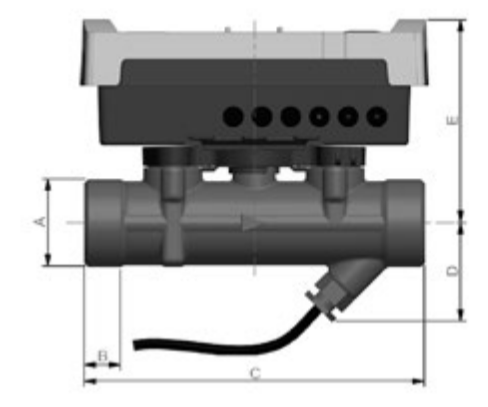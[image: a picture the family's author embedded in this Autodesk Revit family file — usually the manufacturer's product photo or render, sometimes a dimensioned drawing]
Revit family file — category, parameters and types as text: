
# Revit family: Узел квартирный для ГВС и ХВС_Danfoss_ШКСВ
name_source: partatom
category: Арматура трубопроводов
revit_build: Autodesk Revit 2018 (Build: 20170223_1515(x64)
units: mm (PartAtom-declared; Revit-internal decimal feet)

## family parameters
Всегда вертикально = Да
На основе рабочей плоскости = Нет
Общий = Нет
При загрузке вырезать с полостями = Нет
Размер круглого соединителя = Использовать диаметр
Тип детали = Нормальный

## types (2) — shared parameters
ADSK_Единица измерения = шт.
ADSK_Завод-изготовитель = Danfoss
ADSK_Количество = 1
ADSK_Материал = Danfoss__Сталь
URL = https://www.danfoss.com
Изготовитель = Danfoss
Изготовитель (телефон) = +7(495)792-57-57
Разработчик = ООО ПРОРУБИМ
Разработчик (URL) = http://prorubim.com
Разработчик (телефон) = +7(495)649-85-43
Таблица1 = ШКСВ_Обозначение
Таблица2 = ШКСВ_Наименование
Таблица3 = ШКСВ_Код
Таблица4 = ШКСВ_Длина

## per-type parameters (varying)
| type | ADSK_Диаметр условный |
| Узел квартирный для ГВС и ХВС с диаметром Ду15 | 15 мм |
| Узел квартирный для ГВС и ХВС с диаметром Ду20 | 20 мм |
